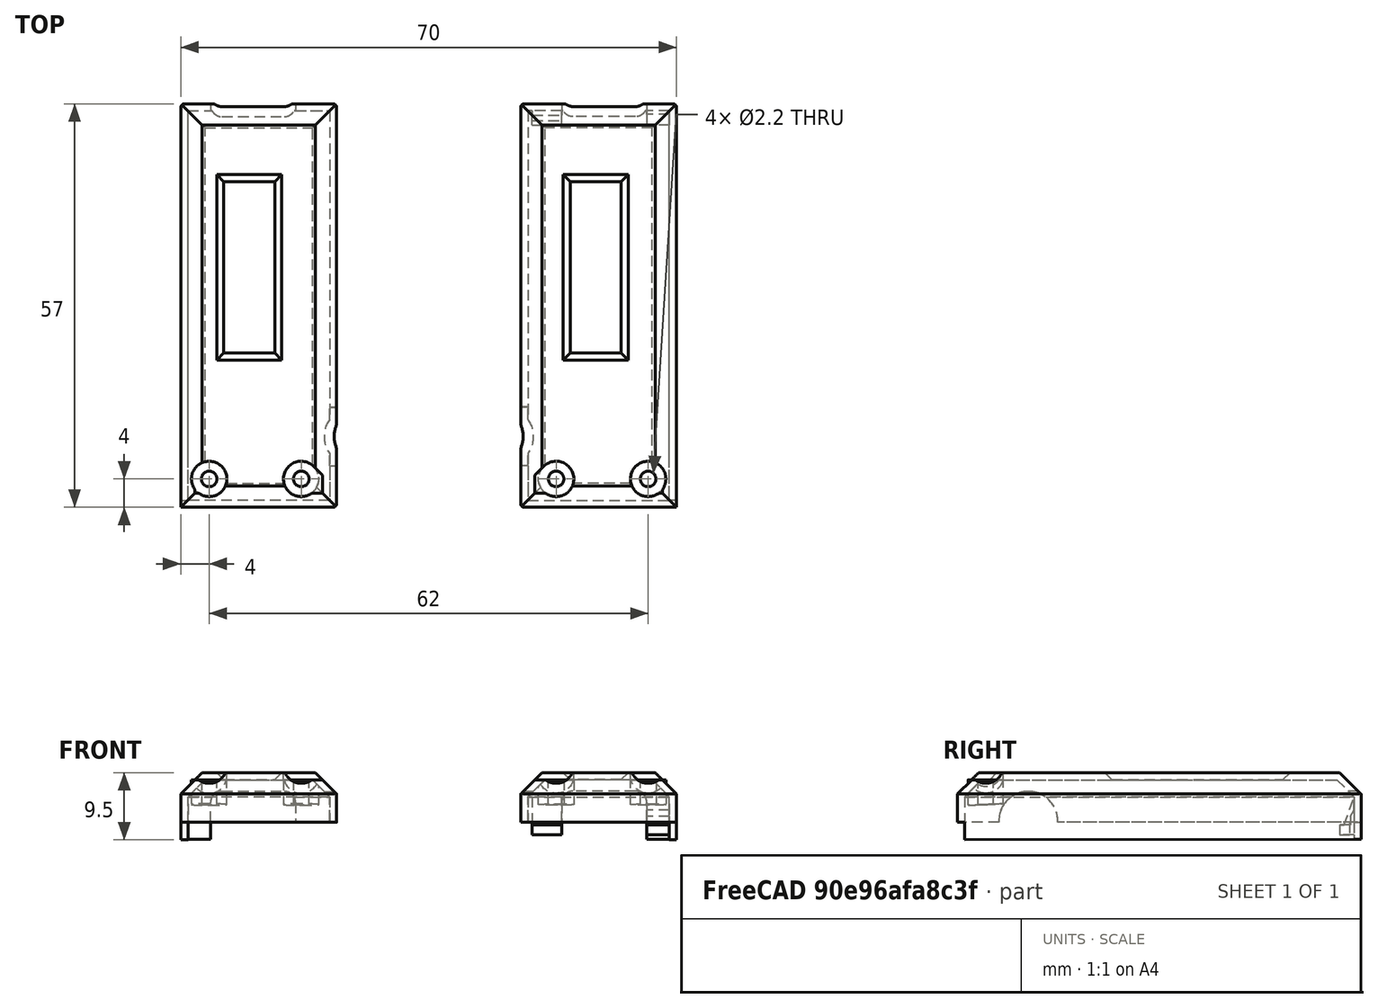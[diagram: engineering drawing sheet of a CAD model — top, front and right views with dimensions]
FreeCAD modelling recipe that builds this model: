
FCSTD DOCUMENT  (FreeCAD 1.0R39285 (Git))
Label: cinque-1.0-cover-OLED
License: All rights reserved
LicenseURL: https://en.wikipedia.org/wiki/All_rights_reserved
objects: Sketcher::SketchObject×13, PartDesign::Pad×6, PartDesign::Pocket×6, PartDesign::Chamfer×2, PartDesign::Thickness×1, PartDesign::Fillet×1, Part::Mirroring×1, Part::Box×1, Part::Cut×1, Part::Chamfer×1, PartDesign::Body×1
note: 79 computed .brp shape members not serialized (recipe doc carries the construction recipe); baked Part::Feature solids carry a one-line shape summary decoded from their .brp

FEATURE [Sketcher::SketchObject] Sketch
  ArcFitTolerance = 1e-06
  AttachmentSupport = -> [XY_Plane001]
  FullyConstrained = true
  MakeInternals = false
  MapMode = 5
  sketch-geometry (5):
    g0: LineSegment StartX=-11 StartY=-28.5 StartZ=0 EndX=11 EndY=-28.5 EndZ=0
    g1: LineSegment StartX=11 StartY=-28.5 StartZ=0 EndX=11 EndY=28.5 EndZ=0
    g2: LineSegment StartX=11 StartY=28.5 StartZ=0 EndX=-11 EndY=28.5 EndZ=0
    g3: LineSegment StartX=-11 StartY=28.5 StartZ=0 EndX=-11 EndY=-28.5 EndZ=0
    g4: GeomPoint [constr] X=0 Y=0 Z=0
  constraints (12):
    c: Coincident(g0,g1)
    c: Coincident(g1,g2)
    c: Coincident(g2,g3)
    c: Coincident(g3,g0)
    c: Horizontal(g0)
    c: Horizontal(g2)
    c: Vertical(g1)
    c: Vertical(g3)
    c: Symmetric(g2,g0,g4)
    c: Distance(g1,g3) = 22
    c: Distance(g0,g2) = 57
    c: Coincident(g4,g-1)
FEATURE [PartDesign::Pad] Pad
  Direction = (0,0,1)
  Length = 7
  Length2 = 10
  Profile = -> Sketch
  ReferenceAxis = -> Sketch [N_Axis]
  Refine = true
  Suppressed = false
  Type = 0
FEATURE [PartDesign::Chamfer] Chamfer
  Angle = 45
  Base = -> Pad [Face6]
  BaseFeature = -> Pad
  ChamferType = 0
  FlipDirection = false
  Refine = true
  Size = 3
  Size2 = 1
  SupportTransform = false
  Suppressed = false
  UseAllEdges = false
FEATURE [PartDesign::Thickness] Thickness
  Base = -> Chamfer [Face4]
  BaseFeature = -> Chamfer
  Intersection = false
  Join = 0
  Mode = 0
  Refine = true
  Reversed = true
  SupportTransform = false
  Suppressed = false
  Value = 1
FEATURE [Sketcher::SketchObject] Sketch001
  ArcFitTolerance = 1e-06
  AttachmentSupport = -> [Thickness]
  ExternalGeometry = -> [Thickness]
  FullyConstrained = true
  MakeInternals = false
  MapMode = 5
  Placement = pos=(-11,0,0) rot=(0.57735,-0.57735,-0.57735;2.0944rad)
  sketch-geometry (1):
    g0: Circle CenterX=18.5 CenterY=0.2 CenterZ=0 NormalX=0 NormalY=0 NormalZ=1 AngleXU=0 Radius=4.15
  constraints (3):
    c: Diameter(g0) = 8.3
    c: Distance(g0,g-3) = 47
    c: Distance(g0,g-1) = 0.2
FEATURE [PartDesign::Pocket] Pocket
  BaseFeature = -> Thickness
  Direction = (1,0,0)
  Length = 5
  Length2 = 5
  Profile = -> Sketch001
  ReferenceAxis = -> Sketch001 [N_Axis]
  Refine = true
  Suppressed = false
  Type = 0
FEATURE [Sketcher::SketchObject] Sketch002
  ArcFitTolerance = 1e-06
  AttachmentSupport = -> [Pocket]
  ExternalGeometry = -> [Pocket]
  FullyConstrained = true
  MakeInternals = false
  MapMode = 5
  Placement = pos=(0,28.5,0) rot=(0,0.707107,0.707107;3.14159rad)
  sketch-geometry (14):
    g0: LineSegment StartX=-6.8 StartY=-1 StartZ=0 EndX=-6.8 EndY=2.8 EndZ=0
    g1: LineSegment StartX=-5.2 StartY=4.4 StartZ=0 EndX=3.6 EndY=4.4 EndZ=0
    g2: LineSegment StartX=5.2 StartY=2.8 StartZ=0 EndX=5.2 EndY=-1 EndZ=0
    g3: LineSegment StartX=3.6 StartY=-2.6 StartZ=0 EndX=-5.2 EndY=-2.6 EndZ=0
    g4: ArcOfCircle CenterX=-5.2 CenterY=2.8 CenterZ=0 NormalX=0 NormalY=0 NormalZ=1 AngleXU=0 Radius=1.6 StartAngle=1.5708 EndAngle=3.14159
    g5: GeomPoint [constr] X=-6.8 Y=4.4 Z=0
    g6: ArcOfCircle CenterX=3.6 CenterY=2.8 CenterZ=0 NormalX=0 NormalY=0 NormalZ=1 AngleXU=0 Radius=1.6 StartAngle=0 EndAngle=1.5708
    g7: GeomPoint [constr] X=5.2 Y=4.4 Z=0
    g8: ArcOfCircle CenterX=3.6 CenterY=-1 CenterZ=0 NormalX=0 NormalY=0 NormalZ=1 AngleXU=0 Radius=1.6 StartAngle=4.71239 EndAngle=6.28319
    g9: GeomPoint [constr] X=5.2 Y=-2.6 Z=0
    g10: ArcOfCircle CenterX=-5.2 CenterY=-1 CenterZ=0 NormalX=0 NormalY=0 NormalZ=1 AngleXU=0 Radius=1.6 StartAngle=3.14159 EndAngle=4.71239
    g11: GeomPoint [constr] X=-6.8 Y=-2.6 Z=0
    g12: GeomPoint [constr] X=-0.8 Y=4.4 Z=0
    g13: GeomPoint [constr] X=5.2 Y=0.9 Z=0
  constraints (30):
    c: Horizontal(g1)
    c: Parallel(g1,g3)
    c: Parallel(g0,g2)
    c: PointOnObject(g5,g0)
    c: PointOnObject(g5,g1)
    c: Tangent(g0,g4) = 1.5708
    c: Tangent(g1,g4) = 1.5708
    c: PointOnObject(g7,g1)
    c: PointOnObject(g7,g2)
    c: Tangent(g1,g6) = 1.5708
    c: Tangent(g2,g6) = 1.5708
    c: PointOnObject(g9,g2)
    c: PointOnObject(g9,g3)
    c: Tangent(g2,g8) = 1.5708
    c: Tangent(g3,g8) = 1.5708
    c: PointOnObject(g11,g0)
    c: PointOnObject(g11,g3)
    c: Tangent(g0,g10) = 1.5708
    c: Tangent(g3,g10) = 1.5708
    c: Perpendicular(g3,g0)
    c: Symmetric(g1,g1,g12)
    c: Distance(g12,g-3) = 11.8
    c: Symmetric(g2,g2,g13)
    c: Distance(g13,g-1) = 0.9
    c: Distance(g2,g0) = 12
    c: Distance(g3,g1) = 7
    c: Radius(g10) = 1.6
    c: Radius(g4) = 1.6
    c: Radius(g6) = 1.6
    c: Radius(g8) = 1.6
FEATURE [PartDesign::Pocket] Pocket001
  BaseFeature = -> Pocket
  Direction = (0,-1,2e-16)
  Length = 5
  Length2 = 5
  Profile = -> Sketch002
  ReferenceAxis = -> Sketch002 [N_Axis]
  Refine = true
  Suppressed = false
  Type = 0
FEATURE [Sketcher::SketchObject] Sketch003
  ArcFitTolerance = 1e-06
  AttachmentOffset = pos=(0,0,6) rot=(0,0,1;0rad)
  AttachmentSupport = -> [XY_Plane001]
  ExternalGeometry = -> [Pocket001]
  FullyConstrained = true
  MakeInternals = false
  MapMode = 5
  Placement = pos=(0,0,6) rot=(0,0,1;0rad)
  sketch-geometry (3):
    g0: LineSegment [constr] StartX=-11 StartY=-24.5 StartZ=0 EndX=11 EndY=-24.5 EndZ=0
    g1: Circle CenterX=-6 CenterY=-24.5 CenterZ=0 NormalX=0 NormalY=0 NormalZ=1 AngleXU=0 Radius=2.5
    g2: Circle CenterX=7 CenterY=-24.5 CenterZ=0 NormalX=0 NormalY=0 NormalZ=1 AngleXU=0 Radius=2.5
  constraints (10):
    c: PointOnObject(g0,g-4)
    c: Horizontal(g0)
    c: Distance(g0,g-3) = 53
    c: Diameter(g1) = 5
    c: PointOnObject(g1,g0)
    c: Distance(g0,g1) = 5
    c: Diameter(g2) = 5
    c: PointOnObject(g2,g0)
    c: DistanceX(g0,g2) = 18
    c: PointOnObject(g0,g-5)
FEATURE [Sketcher::SketchObject] Sketch004
  ArcFitTolerance = 1e-06
  AttachmentOffset = pos=(0,0,7) rot=(0,0,1;0rad)
  AttachmentSupport = -> [XY_Plane001]
  ExternalGeometry = -> [Pocket001]
  FullyConstrained = true
  MakeInternals = false
  MapMode = 5
  Placement = pos=(0,0,7) rot=(0,0,1;0rad)
  sketch-geometry (8):
    g0: LineSegment [constr] StartX=-11 StartY=-24.5 StartZ=0 EndX=11 EndY=-24.5 EndZ=0
    g1: ArcOfCircle CenterX=-6 CenterY=-24.5 CenterZ=0 NormalX=0 NormalY=0 NormalZ=1 AngleXU=0 Radius=2.5 StartAngle=4.71239 EndAngle=8.63938
    g2: ArcOfCircle CenterX=7 CenterY=-24.5 CenterZ=0 NormalX=0 NormalY=0 NormalZ=1 AngleXU=0 Radius=2.5 StartAngle=0 EndAngle=4.71239
    g3: LineSegment StartX=-12.0355 StartY=-27 StartZ=0 EndX=-6 EndY=-27 EndZ=0
    g4: LineSegment StartX=9.5 StartY=-24.5 StartZ=0 EndX=9.5 EndY=-27 EndZ=0
    g5: LineSegment StartX=9.5 StartY=-27 StartZ=0 EndX=7 EndY=-27 EndZ=0
    g6: LineSegment StartX=-7.76777 StartY=-22.7322 StartZ=0 EndX=-12.0355 EndY=-27 EndZ=0
    g7: LineSegment [constr] StartX=-6 StartY=-24.5 StartZ=0 EndX=-7.76777 EndY=-22.7322 EndZ=0
  constraints (26):
    c: PointOnObject(g0,g-4)
    c: Horizontal(g0)
    c: Distance(g0,g-3) = 53
    c: Diameter(g1) = 5
    c: PointOnObject(g1,g0)
    c: Distance(g0,g1) = 5
    c: Diameter(g2) = 5
    c: PointOnObject(g2,g0)
    c: DistanceX(g0,g2) = 18
    c: PointOnObject(g0,g-5)
    c: Horizontal(g3)
    c: Vertical(g3,g1)
    c: Coincident(g1,g3)
    c: PointOnObject(g4,g0)
    c: Coincident(g4,g5)
    c: Vertical(g5,g2)
    c: Perpendicular(g4,g5)
    c: Tangent(g4,g2) = 1.5708
    c: Coincident(g2,g5)
    c: PointOnObject(g2,g0)
    c: Coincident(g6,g3)
    c: Angle(g3,g6) = 0.785398
    c: Coincident(g7,g1)
    c: Coincident(g7,g6)
    c: Angle(g0,g7) = 2.35619
    c: Coincident(g1,g6)
FEATURE [Sketcher::SketchObject] Sketch005
  ArcFitTolerance = 1e-06
  AttachmentOffset = pos=(0,0,7) rot=(0,0,1;0rad)
  AttachmentSupport = -> [XY_Plane001]
  ExternalGeometry = -> [Pocket001]
  FullyConstrained = true
  MakeInternals = false
  MapMode = 5
  Placement = pos=(0,0,7) rot=(0,0,1;0rad)
  sketch-geometry (3):
    g0: LineSegment [constr] StartX=-11 StartY=-24.5 StartZ=0 EndX=11 EndY=-24.5 EndZ=0
    g1: Circle CenterX=-6 CenterY=-24.5 CenterZ=0 NormalX=0 NormalY=0 NormalZ=1 AngleXU=0 Radius=1.1
    g2: Circle CenterX=7 CenterY=-24.5 CenterZ=0 NormalX=0 NormalY=0 NormalZ=1 AngleXU=0 Radius=1.1
  constraints (10):
    c: PointOnObject(g0,g-4)
    c: Horizontal(g0)
    c: Distance(g0,g-3) = 53
    c: Diameter(g1) = 2.2
    c: PointOnObject(g1,g0)
    c: Distance(g0,g1) = 5
    c: Diameter(g2) = 2.2
    c: PointOnObject(g2,g0)
    c: DistanceX(g0,g2) = 18
    c: PointOnObject(g0,g-5)
FEATURE [PartDesign::Pad] Pad001
  BaseFeature = -> Pocket001
  Direction = (0,0,1)
  Length = 3.6
  Length2 = 10
  Profile = -> Sketch003
  ReferenceAxis = -> Sketch003 [N_Axis]
  Refine = true
  Reversed = true
  Suppressed = false
  Type = 0
FEATURE [PartDesign::Pocket] Pocket002
  BaseFeature = -> Pad001
  Direction = (0,0,-1)
  Length = 1
  Length2 = 5
  Profile = -> Sketch004
  ReferenceAxis = -> Sketch004 [N_Axis]
  Refine = true
  Suppressed = false
  Type = 0
FEATURE [PartDesign::Pocket] Pocket003
  BaseFeature = -> Pocket002
  Direction = (0,0,-1)
  Length = 5
  Length2 = 5
  Profile = -> Sketch005
  ReferenceAxis = -> Sketch005 [N_Axis]
  Refine = true
  Suppressed = false
  Type = 0
FEATURE [Sketcher::SketchObject] Sketch006
  ArcFitTolerance = 1e-06
  AttachmentSupport = -> [Pocket003]
  ExternalGeometry = -> [Pocket003]
  FullyConstrained = true
  MakeInternals = false
  MapMode = 5
  Placement = pos=(0,0,7) rot=(0,0,1;0rad)
  sketch-geometry (4):
    g0: LineSegment StartX=-4 StartY=17.5 StartZ=0 EndX=-4 EndY=-6.7 EndZ=0
    g1: LineSegment StartX=-4 StartY=-6.7 StartZ=0 EndX=3.2 EndY=-6.7 EndZ=0
    g2: LineSegment StartX=3.2 StartY=-6.7 StartZ=0 EndX=3.2 EndY=17.5 EndZ=0
    g3: LineSegment StartX=3.2 StartY=17.5 StartZ=0 EndX=-4 EndY=17.5 EndZ=0
  constraints (12):
    c: Coincident(g0,g1)
    c: Coincident(g1,g2)
    c: Coincident(g2,g3)
    c: Coincident(g3,g0)
    c: Vertical(g0)
    c: Vertical(g2)
    c: Horizontal(g1)
    c: Horizontal(g3)
    c: Distance(g0,g-3) = 11
    c: Distance(g0,g-4) = 7
    c: DistanceX(g3,g3) = 7.2
    c: DistanceY(g2,g2) = 24.2
FEATURE [Sketcher::SketchObject] Sketch007
  ArcFitTolerance = 1e-06
  AttachmentSupport = -> [Pocket003]
  FullyConstrained = true
  MakeInternals = false
  MapMode = 5
  Placement = pos=(0,0,0) rot=(1,0,0;3.14159rad)
  sketch-geometry (4):
    g0: LineSegment StartX=11 StartY=-28.5 StartZ=0 EndX=11 EndY=-27.5 EndZ=0
    g1: LineSegment StartX=11 StartY=-27.5 StartZ=0 EndX=6.8 EndY=-27.5 EndZ=0
    g2: LineSegment StartX=6.8 StartY=-27.5 StartZ=0 EndX=6.8 EndY=-28.5 EndZ=0
    g3: LineSegment StartX=6.8 StartY=-28.5 StartZ=0 EndX=11 EndY=-28.5 EndZ=0
  constraints (11):
    c: Coincident(g0,g1)
    c: Coincident(g1,g2)
    c: Coincident(g2,g3)
    c: Coincident(g3,g0)
    c: Vertical(g0)
    c: Vertical(g2)
    c: Horizontal(g1)
    c: Horizontal(g3)
    c: Distance(g0,g2) = 4.2
    c: Distance(g1,g3) = 1
    c: Coincident(g0,g-4)
FEATURE [PartDesign::Pad] Pad002
  BaseFeature = -> Pocket003
  Direction = (0,0,-1)
  Length = 2.4
  Length2 = 10
  Profile = -> Sketch007
  ReferenceAxis = -> Sketch007 [N_Axis]
  Refine = true
  Suppressed = false
  Type = 0
FEATURE [Sketcher::SketchObject] Sketch008
  ArcFitTolerance = 1e-06
  AttachmentSupport = -> [Pad002]
  ExternalGeometry = -> [Pad002]
  FullyConstrained = true
  MakeInternals = false
  MapMode = 5
  Placement = pos=(10,0,0) rot=(0.57735,-0.57735,-0.57735;2.0944rad)
  sketch-geometry (4):
    g0: LineSegment StartX=27 StartY=0 StartZ=0 EndX=27 EndY=2.4 EndZ=0
    g1: LineSegment StartX=27 StartY=2.4 StartZ=0 EndX=22 EndY=2.6 EndZ=0
    g2: LineSegment StartX=22 StartY=2.6 StartZ=0 EndX=22 EndY=0 EndZ=0
    g3: LineSegment StartX=22 StartY=0 StartZ=0 EndX=27 EndY=0 EndZ=0
  constraints (12):
    c: Vertical(g0)
    c: Coincident(g0,g1)
    c: Coincident(g1,g2)
    c: PointOnObject(g2,g-4)
    c: Vertical(g2)
    c: Coincident(g2,g3)
    c: DistanceY(g0,g-3) = 4.6
    c: DistanceY(g1,g-3) = 4.4
    c: DistanceX(g3,g3) = 5
    c: Coincident(g0,g3)
    c: PointOnObject(g0,g-4)
    c: Distance(g0,g-4) = 0.5
FEATURE [PartDesign::Pocket] Pocket005
  BaseFeature = -> Pad002
  Direction = (1,0,0)
  Length = 19
  Length2 = 5
  Profile = -> Sketch008
  ReferenceAxis = -> Sketch008 [N_Axis]
  Refine = true
  Reversed = true
  Suppressed = false
  Type = 0
FEATURE [Sketcher::SketchObject] Sketch009
  ArcFitTolerance = 1e-06
  AttachmentSupport = -> [Pocket005]
  ExternalGeometry = -> [Pocket005]
  FullyConstrained = true
  MakeInternals = false
  MapMode = 5
  Placement = pos=(11,0,0) rot=(0.57735,0.57735,0.57735;2.0944rad)
  sketch-geometry (4):
    g0: LineSegment StartX=27.5 StartY=0 StartZ=0 EndX=27.5 EndY=-2.4 EndZ=0
    g1: LineSegment StartX=27.5 StartY=-2.4 StartZ=0 EndX=-27.5 EndY=-2.5 EndZ=0
    g2: LineSegment StartX=-27.5 StartY=-2.5 StartZ=0 EndX=-27.5 EndY=0 EndZ=0
    g3: LineSegment StartX=-27.5 StartY=0 StartZ=0 EndX=27.5 EndY=0 EndZ=0
  constraints (9):
    c: Coincident(g0,g1)
    c: Coincident(g1,g2)
    c: Vertical(g2)
    c: Coincident(g2,g3)
    c: Coincident(g3,g0)
    c: Coincident(g2,g-3)
    c: Distance(g2,g2) = 2.5
    c: Coincident(g0,g-4)
    c: Coincident(g0,g-4)
FEATURE [PartDesign::Pad] Pad003
  BaseFeature = -> Pocket005
  Direction = (1,0,0)
  Length = 1
  Length2 = 10
  Profile = -> Sketch009
  ReferenceAxis = -> Sketch009 [N_Axis]
  Refine = true
  Reversed = true
  Suppressed = false
  Type = 0
FEATURE [PartDesign::Fillet] Fillet
  Base = -> Pad003 [Edge76,Edge26,Edge1,Edge93]
  BaseFeature = -> Pad003
  Radius = 0.5
  Refine = true
  SupportTransform = false
  Suppressed = false
  UseAllEdges = false
FEATURE [Sketcher::SketchObject] Sketch010
  ArcFitTolerance = 1e-06
  ExternalGeometry = -> [Pocket003]
  FullyConstrained = true
  MakeInternals = false
  MapMode = 5
  Placement = pos=(0,0,7) rot=(0,0,1;0rad)
  sketch-geometry (4):
    g0: LineSegment StartX=-52.95 StartY=17.5 StartZ=0 EndX=-52.95 EndY=-6.7 EndZ=0
    g1: LineSegment StartX=-52.95 StartY=-6.7 StartZ=0 EndX=-45.75 EndY=-6.7 EndZ=0
    g2: LineSegment StartX=-45.75 StartY=-6.7 StartZ=0 EndX=-45.75 EndY=17.5 EndZ=0
    g3: LineSegment StartX=-45.75 StartY=17.5 StartZ=0 EndX=-52.95 EndY=17.5 EndZ=0
  constraints (12):
    c: Coincident(g0,g1)
    c: Coincident(g1,g2)
    c: Coincident(g2,g3)
    c: Coincident(g3,g0)
    c: Vertical(g0)
    c: Vertical(g2)
    c: Horizontal(g1)
    c: Horizontal(g3)
    c: Distance(g0,g-3) = 11
    c: DistanceX(g3,g3) = 7.2
    c: DistanceY(g2,g2) = 24.2
    c: Distance(g2,g-5) = 8.75
FEATURE [Part::Mirroring] Part__Mirroring  label="Fillet (Mirror #1)"
  Base = (-24,0,0)
  Normal = (1,0,0)
  Source = -> Fillet
FEATURE [Part::Box] Box  label="Cube"
  AttacherType = Attacher::AttachEngine3D
  Height = 10
  Length = 7.2
  Placement = pos=(-52.95,-6.7,0) rot=(0,0,1;0rad)
  Width = 24.2
FEATURE [Part::Cut] Cut
  Base = -> Part__Mirroring
  Refine = true
  Tool = -> Box
FEATURE [Part::Chamfer] Chamfer001
  Base = -> Cut
  EdgeLinks = -> Cut [Edge63,Edge64,Edge65,Edge66]
  Edges = 4 edges r=0.99: [Edge63,Edge64,Edge65,Edge66]
FEATURE [PartDesign::Pocket] Pocket006
  BaseFeature = -> Fillet
  Direction = (0,0,-1)
  Length = 5
  Length2 = 5
  Profile = -> Sketch006
  ReferenceAxis = -> Sketch006 [N_Axis]
  Refine = true
  Suppressed = false
  Type = 0
FEATURE [PartDesign::Chamfer] Chamfer002
  Angle = 45
  Base = -> Pocket006 [Edge66,Edge65,Edge64,Edge63]
  BaseFeature = -> Pocket006
  ChamferType = 0
  FlipDirection = false
  Refine = true
  Size = 0.99
  Size2 = 1
  SupportTransform = false
  Suppressed = false
  UseAllEdges = false
FEATURE [Sketcher::SketchObject] Sketch011
  ArcFitTolerance = 1e-06
  AttachmentOffset = pos=(0,0,0.6) rot=(0,0,1;0rad)
  AttachmentSupport = -> [Chamfer002]
  ExternalGeometry = -> [Chamfer002]
  FullyConstrained = true
  MakeInternals = false
  MapMode = 5
  Placement = pos=(-9.4,0,0) rot=(0.57735,0.57735,0.57735;2.0944rad)
  sketch-geometry (7):
    g0: LineSegment StartX=27.5 StartY=3.58579 StartZ=0 EndX=27.5 EndY=0 EndZ=0
    g1: LineSegment StartX=25.5 StartY=-1.8 StartZ=0 EndX=26.9 EndY=-1.8 EndZ=0
    g2: LineSegment StartX=27.5 StartY=0 StartZ=0 EndX=26.9 EndY=0 EndZ=0
    g3: LineSegment StartX=26.9 StartY=0 StartZ=0 EndX=26.9 EndY=-1.8 EndZ=0
    g4: LineSegment StartX=25.5 StartY=-1.8 StartZ=0 EndX=25.5 EndY=-0.4 EndZ=0
    g5: LineSegment StartX=25.5 StartY=-0.4 StartZ=0 EndX=26.1 EndY=-0.4 EndZ=0
    g6: LineSegment StartX=26.1 StartY=-0.4 StartZ=0 EndX=27.5 EndY=3.58579 EndZ=0
  constraints (20):
    c: PointOnObject(g0,g-1)
    c: Vertical(g0)
    c: Horizontal(g1)
    c: Coincident(g0,g2)
    c: PointOnObject(g2,g-1)
    c: Coincident(g2,g3)
    c: Coincident(g3,g1)
    c: Coincident(g1,g4)
    c: Vertical(g4)
    c: Coincident(g4,g5)
    c: Horizontal(g5)
    c: Coincident(g5,g6)
    c: DistanceX(g2,g2) = 0.6
    c: Distance(g1,g0) = 2
    c: Distance(g-1,g5) = 0.4
    c: DistanceY(g4,g4) = 1.4
    c: Coincident(g6,g0)
    c: DistanceX(g5,g2) = 0.8
    c: Vertical(g3)
    c: Coincident(g0,g-3)
FEATURE [PartDesign::Pad] Pad004
  BaseFeature = -> Chamfer002
  Direction = (1,0,0)
  Length = 4.2
  Length2 = 10
  Profile = -> Sketch011
  ReferenceAxis = -> Sketch011 [N_Axis]
  Refine = true
  Suppressed = false
  Type = 0
FEATURE [Sketcher::SketchObject] Sketch012
  ArcFitTolerance = 1e-06
  AttachmentSupport = -> [Pad004]
  ExternalGeometry = -> [Pad004]
  FullyConstrained = true
  MakeInternals = false
  MapMode = 5
  Placement = pos=(10,0,0) rot=(0.57735,-0.57735,-0.57735;2.0944rad)
  sketch-geometry (6):
    g0: LineSegment StartX=-27.5 StartY=1.7 StartZ=0 EndX=-27.5 EndY=-1.8 EndZ=0
    g1: LineSegment StartX=-27.5 StartY=-1.8 StartZ=0 EndX=-25.5 EndY=-1.8 EndZ=0
    g2: LineSegment StartX=-27 StartY=0.8 StartZ=0 EndX=-27.5 EndY=1.7 EndZ=0
    g3: LineSegment StartX=-25.5 StartY=-0.4 StartZ=0 EndX=-25.5 EndY=-1.8 EndZ=0
    g4: LineSegment StartX=-27 StartY=0.8 StartZ=0 EndX=-27 EndY=-0.4 EndZ=0
    g5: LineSegment StartX=-27 StartY=-0.4 StartZ=0 EndX=-25.5 EndY=-0.4 EndZ=0
  constraints (18):
    c: Vertical(g0)
    c: Coincident(g0,g1)
    c: Horizontal(g1)
    c: Coincident(g2,g0)
    c: Vertical(g3)
    c: DistanceX(g1,g1) = 2
    c: Coincident(g2,g4)
    c: Vertical(g4)
    c: Coincident(g4,g5)
    c: Coincident(g5,g3)
    c: Horizontal(g5)
    c: Coincident(g1,g3)
    c: DistanceY(g3,g3) = 1.4
    c: Distance(g4,g0) = 0.5
    c: DistanceY(g0,g0) = 3.5
    c: DistanceY(g4,g4) = 1.2
    c: PointOnObject(g0,g-4)
    c: Distance(g-1,g5) = 0.4
FEATURE [PartDesign::Pad] Pad005
  BaseFeature = -> Pad004
  Direction = (-1,0,0)
  Length = 3.2
  Length2 = 10
  Profile = -> Sketch012
  ReferenceAxis = -> Sketch012 [N_Axis]
  Refine = true
  Suppressed = false
  Type = 0
FEATURE [PartDesign::Body] Body001
  AllowCompound = false
  Group = -> [Sketch,Pad,Chamfer,Thickness,Sketch001,Pocket,Sketch002,Pocket001,Sketch003,Sketch004,Sketch005,Pad001,Pocket002,Pocket003,Sketch006,Sketch007,Pad002,Sketch008,Pocket005,Sketch009,Pad003,Fillet,Pocket006,Chamfer002,Sketch011,Pad004,Sketch012,Pad005]
  Origin = -> Origin001
  Tip = -> Pad005
